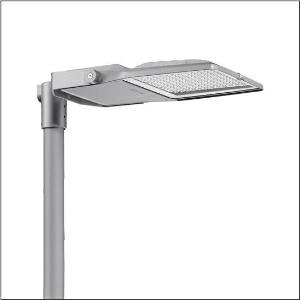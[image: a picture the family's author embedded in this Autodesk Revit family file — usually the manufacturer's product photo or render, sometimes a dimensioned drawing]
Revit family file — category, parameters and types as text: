
# Revit family: floodlight_fl_21_iq_midi___pl64_5xa7782e4e3a_6d1b
name_source: partatom
category: Lighting Fixtures
units: mm (PartAtom-declared; Revit-internal decimal feet)

## family parameters
Cut with Voids When Loaded = No
Host = Face
Light Source = No
Part Type = Normal
Room Calculation Point = No
Round Connector Dimension = Use Diameter
Shared = No

## types (1)
- --- (1 x LED, 27050 lm, 208.1 W, 4000K)
    Apparent Load = 208 VA
    CIE Flux Codes = 28 80 98 100 100
    Color Rendering = 70
    Color Temperature = 4000K
    Default Elevation = 1800 mm
    Description = Floodlight FL 21 iQ midi, floodlight, primary light control with lens, of PMMA, primary optical cover: protective disc, of toughened safety glass, transparent, light distribution: PL64, light emission: direct distribution, installation type: surface-mounted, LED, High Power LED, rated luminous flux: 27.050lm, luminous efficacy: 130lm/W, light colour: 740, colour temperature: 4000K, control gear: ECG iQ, control: optimised constant luminous flux control (CLO 2.0), Desk-Remote (wireless, voltage-free reading and setting of iQ features in the workshop via application-optimized NFC function/RFID function), Smart-Wire, Night-Set, Temp-Guard, Auto-Match, Street-Remote, with terminal, 6-pole, mains connection: 220..240V, AC, 50/60Hz, start of lifetime: 208W, end of service life: 227W, reduction: 90W, luminaire housing, of diecast aluminium, powder-coated, Siteco® metallic grey (DB 702S), corrosivity category C5 mid according to DIN EN ISO 12944, sealing non-destructively replaceable, please order mast flange separately, mast bracket, of steel, galvanised, powder-coated, Siteco® metallic grey (DB 702S), protection rating (complete): IP66, insulation class (complete): insulation class II (safety insulation), certification: CE, protection symbol: D, impact resistance: IK08, permissible operating ambient temperature: -40..+40°C, permissible operating ambient temperature for outdoor applications: -40..+50°C, standard: DIN EN 12944, LABS conformity tested according to VDMA 24364:2018-05, packaging unit: 1 piece

Light Distribution: PL64
    Height = 76 mm
    Lamp = 1 x LED
    Lamp Light Flux = 27050 lm
    Lamp Power = 208.1 W
    Lamp count = 1
    Length = 657 mm
    Luminous efficacy = 130 lm/W
    Manufacturer = Siteco
    ModVariant = No
    Model = 5XA7782E4E3A
    Number of Poles = 1
    OnlyDefault = Yes
    Power Factor = 1
    Product Name = Floodlight FL 21 iQ midi | PL64
    Product group = floodlight | pylon annexe
    ProductGroupID = 6200
    Protection Class = Protection class II
    Protection Degree = IP 66
    RLX_Detail_Level = 1
    RLX_Emergency_Light_Flux = 0 lm
    RLX_Emergency_Type = 0
    RLX_Emergency_Type_DB = No
    RlxData = <blob elided: 153705 chars, md5=18d5ce74>
    Socket = socket
    Standby Power = 0 W
    System Light Flux = 27050 lm
    System Power = 208 W
    Type Comments = factory setting: luminous flux: 100 % | dim-lin: 254 | 710 mA
    Type Image = l_1007123.jpg
    URL = http://relux.com
    VarID = @adj_037109
    Voltage = 0 V
    Weight = 0.00 kg
    Width = 442 mm

## geometry (parser evidence)
native form markers: Blend x4, Sweep x16
no freeform markers — native parametric forms only
